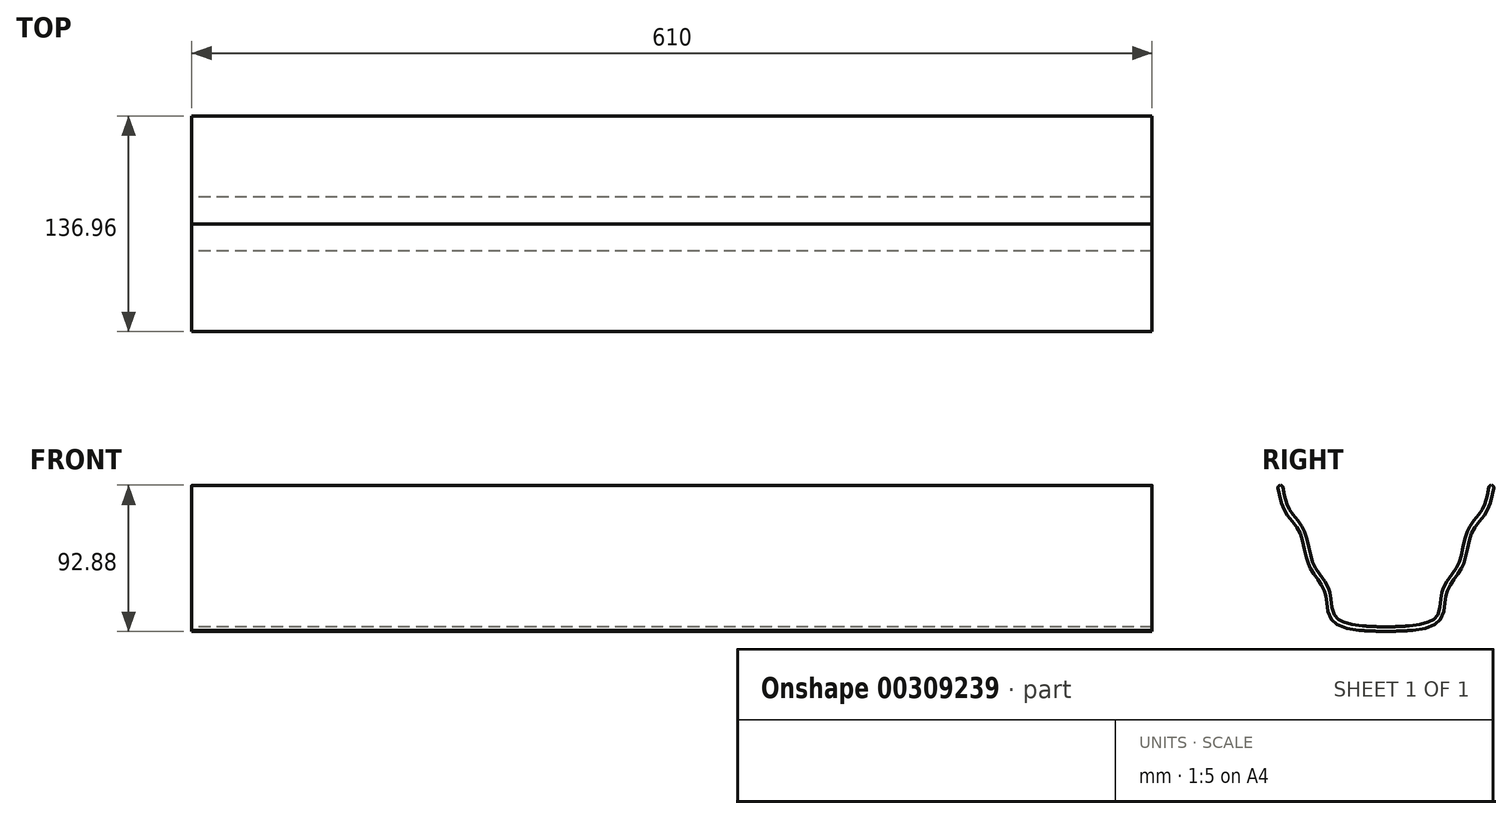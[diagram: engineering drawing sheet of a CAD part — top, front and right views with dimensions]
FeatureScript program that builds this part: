
annotation { "Feature Type Name" : "Feature", "Feature Type Description" : "" }
export const myFeature = defineFeature(function(context is Context, id is Id, definition is map)
    precondition{}
    {
        {
            var Q0;
            Q0=qCreatedBy(makeId("Right.planeOp"),FACE);
            var sketch = newSketch(context, id + "F0", { "sketchPlane" : qUnion([Q0])});
            skPoint(sketch, "E0.visualSharp", {"position": v(-120, 0) * mm});
            skPoint(sketch, "E1.start.orphan", {"position": v(-75, 100) * mm});
            skPoint(sketch, "E2.visualSharp", {"position": v(-6.04, 102.86) * mm});
            skPoint(sketch, "E3.visualSharp", {"position": v(-10.5, 102.86) * mm});
            skPoint(sketch, "E4.visualSharp", {"position": v(-11.4, 100) * mm});
            skPoint(sketch, "E5.visualSharp", {"position": v(-13.5, 100) * mm});
            skPoint(sketch, "E6.visualSharp", {"position": v(-13.5, 105.86) * mm});
            skPoint(sketch, "E7.visualSharp", {"position": v(0, 105.86) * mm});
            skFitSpline(sketch, "E8.0", {"points": [v(-6.54, 100.08) * mm, v(-6.77, 98.71) * mm, v(-7.28, 95.97) * mm, v(-8.25, 91.96) * mm, v(-9.3, 88.8) * mm, v(-10.34, 86.42) * mm, v(-11.23, 84.72) * mm, v(-12.24, 83.13) * mm, v(-13.73, 81.1) * mm, v(-15.77, 78.63) * mm, v(-17.8, 76.06) * mm, v(-19.27, 73.8) * mm, v(-20.25, 71.97) * mm, v(-21.07, 69.97) * mm, v(-21.96, 67.13) * mm, v(-22.82, 63.34) * mm, v(-23.59, 59.42) * mm, v(-24.3, 56.33) * mm, v(-24.92, 54.08) * mm, v(-25.53, 52.27) * mm, v(-26.1, 50.88) * mm, v(-26.73, 49.54) * mm, v(-27.62, 47.93) * mm, v(-28.81, 46.07) * mm, v(-30.09, 44.26) * mm, v(-31.39, 42.47) * mm, v(-32.67, 40.67) * mm, v(-33.88, 38.82) * mm, v(-34.98, 36.9) * mm, v(-35.74, 35.2) * mm, v(-36.25, 33.79) * mm, v(-36.66, 32.32) * mm, v(-37.03, 30.42) * mm, v(-37.34, 28.09) * mm, v(-37.7, 24.96) * mm, v(-38.28, 21.12) * mm, v(-39.59, 17.7) * mm, v(-41.41, 15.35) * mm, v(-43.88, 13.3) * mm, v(-48.46, 11.35) * mm, v(-55.7, 9.88) * mm, v(-64.02, 9.14) * mm, v(-72.8, 8.94) * mm, v(-79.97, 9.08) * mm, v(-85.32, 9.28) * mm, v(-89.06, 9.45) * mm, v(-92.44, 9.63) * mm, v(-95.4, 9.79) * mm, v(-97.85, 9.9) * mm, v(-99.74, 9.94) * mm, v(-101.2, 9.95) * mm, v(-102.31, 9.92) * mm, v(-103.2, 9.9) * mm, v(-103.7, 9.87) * mm, v(-103.96, 9.87) * mm]});
            skFitSpline(sketch, "E8.1", {"points": [v(-143.46, 100.08) * mm, v(-143.23, 98.71) * mm, v(-142.72, 95.97) * mm, v(-141.75, 91.96) * mm, v(-140.7, 88.8) * mm, v(-139.66, 86.42) * mm, v(-138.77, 84.72) * mm, v(-137.76, 83.13) * mm, v(-136.27, 81.1) * mm, v(-134.23, 78.63) * mm, v(-132.2, 76.06) * mm, v(-130.73, 73.8) * mm, v(-129.75, 71.97) * mm, v(-128.93, 69.97) * mm, v(-128.04, 67.13) * mm, v(-127.18, 63.34) * mm, v(-126.41, 59.42) * mm, v(-125.7, 56.33) * mm, v(-125.08, 54.08) * mm, v(-124.47, 52.27) * mm, v(-123.9, 50.88) * mm, v(-123.27, 49.54) * mm, v(-122.38, 47.93) * mm, v(-121.19, 46.07) * mm, v(-119.91, 44.26) * mm, v(-118.61, 42.47) * mm, v(-117.33, 40.67) * mm, v(-116.12, 38.82) * mm, v(-115.02, 36.9) * mm, v(-114.26, 35.2) * mm, v(-113.75, 33.79) * mm, v(-113.34, 32.32) * mm, v(-112.97, 30.42) * mm, v(-112.66, 28.09) * mm, v(-112.3, 24.96) * mm, v(-111.72, 21.12) * mm, v(-110.41, 17.7) * mm, v(-108.59, 15.35) * mm, v(-106.12, 13.3) * mm, v(-101.54, 11.35) * mm, v(-94.3, 9.88) * mm, v(-85.98, 9.14) * mm, v(-77.2, 8.94) * mm, v(-70.03, 9.08) * mm, v(-64.68, 9.28) * mm, v(-60.94, 9.45) * mm, v(-57.56, 9.63) * mm, v(-54.6, 9.79) * mm, v(-52.15, 9.9) * mm, v(-50.26, 9.94) * mm, v(-48.8, 9.95) * mm, v(-47.69, 9.92) * mm, v(-46.8, 9.9) * mm, v(-46.3, 9.87) * mm, v(-46.04, 9.87) * mm]});
            skFitSpline(sketch, "E9.0", {"points": [v(-9.5, 100.59) * mm, v(-9.72, 99.24) * mm, v(-10.22, 96.58) * mm, v(-10.98, 93.4) * mm, v(-11.73, 91.02) * mm, v(-12.35, 89.32) * mm, v(-12.94, 87.98) * mm, v(-13.45, 86.96) * mm, v(-13.84, 86.24) * mm, v(-14.27, 85.53) * mm, v(-14.88, 84.6) * mm, v(-15.74, 83.44) * mm, v(-16.87, 82) * mm, v(-18.1, 80.51) * mm, v(-19.36, 78.93) * mm, v(-20.42, 77.5) * mm, v(-21.24, 76.27) * mm, v(-21.84, 75.31) * mm, v(-22.4, 74.3) * mm, v(-22.95, 73.22) * mm, v(-23.44, 72.1) * mm, v(-24.02, 70.59) * mm, v(-24.63, 68.65) * mm, v(-25.23, 66.3) * mm, v(-25.75, 63.93) * mm, v(-26.22, 61.58) * mm, v(-26.7, 59.28) * mm, v(-27.21, 57.06) * mm, v(-27.7, 55.3) * mm, v(-28.12, 53.96) * mm, v(-28.47, 53) * mm, v(-28.85, 52.08) * mm, v(-29.4, 50.92) * mm, v(-30.19, 49.48) * mm, v(-31.3, 47.76) * mm, v(-32.52, 46.02) * mm, v(-33.82, 44.23) * mm, v(-35.14, 42.37) * mm, v(-36.44, 40.4) * mm, v(-37.45, 38.63) * mm, v(-38.17, 37.12) * mm, v(-38.59, 36.13) * mm, v(-38.89, 35.32) * mm, v(-39.1, 34.7) * mm, v(-39.29, 34.06) * mm, v(-39.52, 33.2) * mm, v(-39.75, 32.15) * mm, v(-40.05, 30.48) * mm, v(-40.32, 28.44) * mm, v(-40.6, 26.1) * mm, v(-40.9, 23.9) * mm, v(-41.3, 21.91) * mm, v(-41.86, 20.18) * mm, v(-42.6, 18.7) * mm, v(-43.42, 17.67) * mm, v(-44.25, 16.9) * mm, v(-44.99, 16.36) * mm, v(-45.9, 15.82) * mm, v(-46.97, 15.3) * mm, v(-48.21, 14.82) * mm, v(-50.05, 14.21) * mm, v(-52.68, 13.56) * mm, v(-56.25, 12.95) * mm, v(-60.13, 12.5) * mm, v(-65.6, 12.1) * mm, v(-72.8, 11.94) * mm, v(-79.89, 12.08) * mm, v(-85.2, 12.28) * mm, v(-88.9, 12.45) * mm, v(-92.28, 12.63) * mm, v(-95.25, 12.78) * mm, v(-97.32, 12.87) * mm, v(-98.72, 12.92) * mm, v(-99.95, 12.94) * mm, v(-101.22, 12.95) * mm, v(-102.4, 12.92) * mm, v(-103.32, 12.89) * mm, v(-103.79, 12.87) * mm, v(-104, 12.87) * mm]});
            skFitSpline(sketch, "E9.1", {"points": [v(-140.5, 100.59) * mm, v(-140.28, 99.24) * mm, v(-139.78, 96.58) * mm, v(-139.02, 93.4) * mm, v(-138.27, 91.02) * mm, v(-137.65, 89.32) * mm, v(-137.06, 87.98) * mm, v(-136.55, 86.96) * mm, v(-136.16, 86.24) * mm, v(-135.73, 85.53) * mm, v(-135.12, 84.6) * mm, v(-134.26, 83.44) * mm, v(-133.13, 82) * mm, v(-131.9, 80.51) * mm, v(-130.64, 78.93) * mm, v(-129.58, 77.5) * mm, v(-128.76, 76.27) * mm, v(-128.16, 75.31) * mm, v(-127.6, 74.3) * mm, v(-127.05, 73.22) * mm, v(-126.56, 72.1) * mm, v(-125.98, 70.59) * mm, v(-125.37, 68.65) * mm, v(-124.77, 66.3) * mm, v(-124.25, 63.93) * mm, v(-123.78, 61.58) * mm, v(-123.3, 59.28) * mm, v(-122.79, 57.06) * mm, v(-122.3, 55.3) * mm, v(-121.88, 53.96) * mm, v(-121.53, 53) * mm, v(-121.15, 52.08) * mm, v(-120.6, 50.92) * mm, v(-119.81, 49.48) * mm, v(-118.7, 47.76) * mm, v(-117.48, 46.02) * mm, v(-116.18, 44.23) * mm, v(-114.86, 42.37) * mm, v(-113.56, 40.4) * mm, v(-112.55, 38.63) * mm, v(-111.83, 37.12) * mm, v(-111.41, 36.13) * mm, v(-111.11, 35.32) * mm, v(-110.9, 34.7) * mm, v(-110.71, 34.06) * mm, v(-110.48, 33.2) * mm, v(-110.25, 32.15) * mm, v(-109.95, 30.48) * mm, v(-109.68, 28.44) * mm, v(-109.4, 26.1) * mm, v(-109.1, 23.9) * mm, v(-108.7, 21.91) * mm, v(-108.14, 20.18) * mm, v(-107.4, 18.7) * mm, v(-106.58, 17.67) * mm, v(-105.75, 16.9) * mm, v(-105.01, 16.36) * mm, v(-104.1, 15.82) * mm, v(-103.03, 15.3) * mm, v(-101.79, 14.82) * mm, v(-99.95, 14.21) * mm, v(-97.32, 13.56) * mm, v(-93.75, 12.95) * mm, v(-89.87, 12.5) * mm, v(-84.4, 12.1) * mm, v(-77.2, 11.94) * mm, v(-70.11, 12.08) * mm, v(-64.8, 12.28) * mm, v(-61.1, 12.45) * mm, v(-57.72, 12.63) * mm, v(-54.75, 12.78) * mm, v(-52.68, 12.87) * mm, v(-51.28, 12.92) * mm, v(-50.05, 12.94) * mm, v(-48.78, 12.95) * mm, v(-47.6, 12.92) * mm, v(-46.68, 12.89) * mm, v(-46.21, 12.87) * mm, v(-46, 12.87) * mm]});
            skArc(sketch, "E10", {"start": v(-143.46, 100.08) * mm, "mid": v(-142.24, 101.81) * mm, "end": v(-140.5, 100.59) * mm});
            skArc(sketch, "E11", {"start": v(-9.5, 100.59) * mm, "mid": v(-7.76, 101.81) * mm, "end": v(-6.54, 100.08) * mm});
            skPoint(sketch, "E12.1.internal.orphan", {"position": v(-143.96, 102.15) * mm});
            skPoint(sketch, "E12.4.internal.orphan", {"position": v(-136, 100) * mm});
            skPoint(sketch, "E12.9.internal.orphan", {"position": v(-143.96, 107.02) * mm});
            skPoint(sketch, "E13.start.orphan", {"position": v(-150, 100) * mm});
            skPoint(sketch, "E14.start.orphan", {"position": v(-143.96, 100) * mm});
            skPoint(sketch, "E15.end.orphan", {"position": v(0, 100) * mm});
            skPoint(sketch, "E16.start.orphan", {"position": v(-6.04, 100) * mm});
            skSolve(sketch);
        }
        {
            var Q0;
            Q0=makeQuery(id+"F0.imprint","IMPRINT",FACE,{"disambiguationData":[TD([[makeQuery(id+"F0.imprint","IMPRINT",EDGE,{"derivedFrom":sQuery(id+"F0.wireOp",EDGE,"E8.0")}),-1.0]])]});
            extrude(context, id + "F1", {"entities" : qUnion([Q0]), "depth" : 610 * mm});
        }
    });
